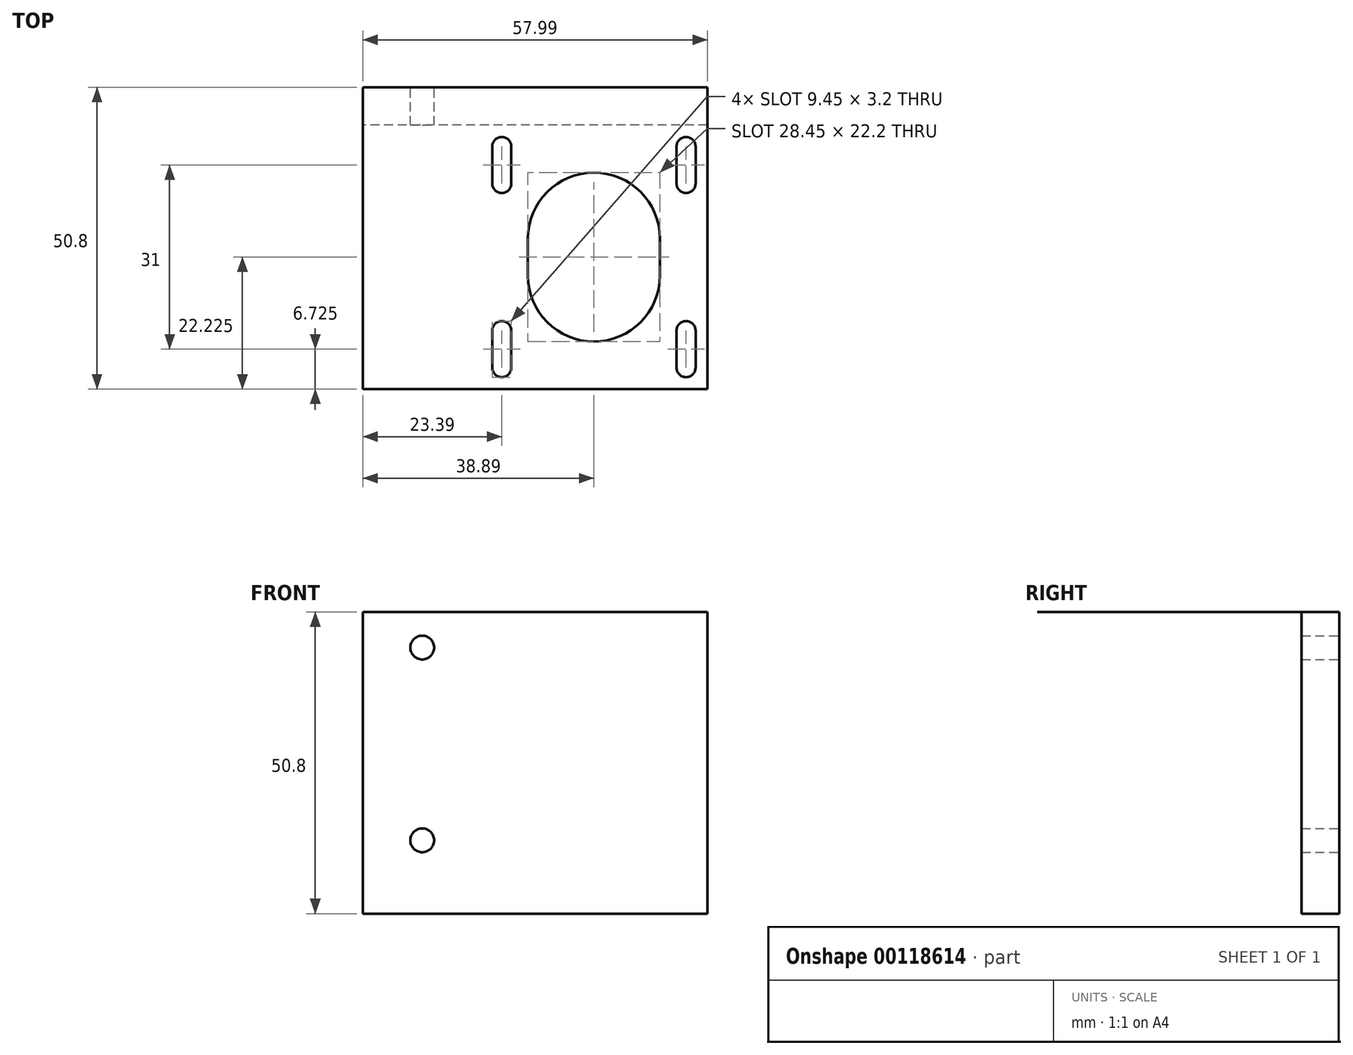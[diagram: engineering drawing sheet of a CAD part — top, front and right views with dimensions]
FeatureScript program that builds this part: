
annotation { "Feature Type Name" : "Feature", "Feature Type Description" : "" }
export const myFeature = defineFeature(function(context is Context, id is Id, definition is map)
    precondition{}
    {
        {
            var Q0;
            Q0=qCreatedBy(makeId("Top.planeOp"),FACE);
            var sketch = newSketch(context, id + "F0", { "sketchPlane" : qUnion([Q0])});
            skCircle(sketch, "E0", {"center": v(0, 0) * mm, "radius": 11.1 * mm});
            skCircle(sketch, "E1", {"center": v(-15.5, -15.5) * mm, "radius": 1.6 * mm});
            skCircle(sketch, "E2", {"center": v(-15.5, 15.5) * mm, "radius": 1.6 * mm});
            skCircle(sketch, "E3", {"center": v(15.5, 15.5) * mm, "radius": 1.6 * mm});
            skCircle(sketch, "E4", {"center": v(15.5, -15.5) * mm, "radius": 1.6 * mm});
            skLineSegment(sketch, "E5", {"start": v(15.5, -15.5) * mm, "end": v(-15.5, -15.5) * mm, "construction": true});
            skPoint(sketch, "E6", {"position": v(0, -15.5) * mm});
            skLineSegment(sketch, "E7", {"start": v(15.5, 15.5) * mm, "end": v(15.5, -15.5) * mm, "construction": true});
            skPoint(sketch, "E8", {"position": v(15.5, 0) * mm});
            skLineSegment(sketch, "E9.bottom", {"start": v(-38.9, 25.45) * mm, "end": v(19.1, 25.45) * mm});
            skLineSegment(sketch, "E9.top", {"start": v(-38.89, -25.35) * mm, "end": v(19.1, -25.35) * mm});
            skLineSegment(sketch, "E9.left", {"start": v(-38.9, 25.45) * mm, "end": v(-38.89, -25.35) * mm});
            skLineSegment(sketch, "E9.right", {"start": v(19.1, 25.45) * mm, "end": v(19.1, -25.35) * mm});
            skLineSegment(sketch, "E10", {"start": v(19.1, 19.1) * mm, "end": v(-38.9, 19.1) * mm});
            skCircle(sketch, "E11", {"center": v(0, -6.25) * mm, "radius": 11.1 * mm});
            skLineSegment(sketch, "E12", {"start": v(-11.1, -6.25) * mm, "end": v(-11.1, 0) * mm});
            skLineSegment(sketch, "E13", {"start": v(11.1, 0) * mm, "end": v(11.1, -6.25) * mm});
            skLineSegment(sketch, "E14", {"start": v(0, 0) * mm, "end": v(0, -6.25) * mm, "construction": true});
            skCircle(sketch, "E15", {"center": v(-15.5, 9.25) * mm, "radius": 1.6 * mm});
            skCircle(sketch, "E16", {"center": v(-15.5, -21.75) * mm, "radius": 1.6 * mm});
            skCircle(sketch, "E17", {"center": v(15.5, -21.75) * mm, "radius": 1.6 * mm});
            skCircle(sketch, "E18", {"center": v(15.5, 9.25) * mm, "radius": 1.6 * mm});
            skLineSegment(sketch, "E19", {"start": v(-15.5, 15.5) * mm, "end": v(-15.5, 9.25) * mm, "construction": true});
            skLineSegment(sketch, "E20", {"start": v(-15.5, -15.5) * mm, "end": v(-15.5, -21.75) * mm, "construction": true});
            skLineSegment(sketch, "E21", {"start": v(-17.1, 15.5) * mm, "end": v(-17.1, 9.25) * mm});
            skLineSegment(sketch, "E22", {"start": v(-13.9, 15.5) * mm, "end": v(-13.9, 9.25) * mm});
            skLineSegment(sketch, "E23", {"start": v(13.9, 15.5) * mm, "end": v(13.9, 9.25) * mm});
            skLineSegment(sketch, "E24", {"start": v(17.1, 15.5) * mm, "end": v(17.1, 9.25) * mm});
            skLineSegment(sketch, "E25", {"start": v(13.9, -21.75) * mm, "end": v(13.9, -15.5) * mm});
            skLineSegment(sketch, "E26", {"start": v(17.1, -15.5) * mm, "end": v(17.1, -21.75) * mm});
            skLineSegment(sketch, "E27", {"start": v(-17.1, -15.5) * mm, "end": v(-17.1, -21.75) * mm});
            skLineSegment(sketch, "E28", {"start": v(-13.9, -15.5) * mm, "end": v(-13.9, -21.75) * mm});
            skCircle(sketch, "E29", {"center": v(0, 0) * mm, "radius": 6.37 * mm, "construction": true});
            skPoint(sketch, "E30", {"position": v(-28.9, 25.45) * mm});
            skLineSegment(sketch, "E31", {"start": v(-6.37, 5) * mm, "end": v(-6.36, -5.45) * mm});
            skLineSegment(sketch, "E32", {"start": v(-18.9, 25.45) * mm, "end": v(-18.89, -25.35) * mm, "construction": true});
            skSolve(sketch);
        }
        {
            var Q0;
            {var subQ0=sQuery(id+"F0.wireOp",EDGE,"E9.bottom");Q0=makeQuery(id+"F0.imprint","IMPRINT",FACE,{"disambiguationData":[TD([[makeQuery(id+"F0.imprint","IMPRINT",EDGE,{"derivedFrom":subQ0}),-1.0]])]});}
            var Q1;
            {var subQ15=sQuery(id+"F0.wireOp",EDGE,"E9.top");Q1=makeQuery(id+"F0.imprint","IMPRINT",FACE,{"disambiguationData":[TD([[makeQuery(id+"F0.imprint","IMPRINT",EDGE,{"derivedFrom":subQ15}),1.0]])]});}
            extrude(context, id + "F1", {"entities" : qUnion([Q0, Q1]), "depth" : 1 / 101.6 * mm});
        }
        {
            var Q0;
            {var subQ0=sQuery(id+"F0.wireOp",EDGE,"E9.bottom");Q0=makeQuery(id+"F0.imprint","IMPRINT",FACE,{"disambiguationData":[TD([[makeQuery(id+"F0.imprint","IMPRINT",EDGE,{"derivedFrom":subQ0}),-1.0]])]});}
            extrude(context, id + "F2", {"entities" : qUnion([Q0]), "operationType" : NewBodyOperationType.ADD, "oppositeDirection" : true, "depth" : 50.8 * mm - 1 / 101.6 * mm});
        }
        {
            var Q0;
            {var subQ0=sQuery(id+"F0.wireOp",EDGE,"E9.bottom");Q0=makeQuery(id+"F2.boolean.opBoolean","MERGE",FACE,{"derivedFrom":[makeQuery(id+"F1.opExtrude","SWEPT_FACE",FACE,{"disambiguationData":[OSD([subQ0])]}),makeQuery(id+"F2.opExtrude","SWEPT_FACE",FACE,{"disambiguationData":[OSD([subQ0])]})]});}
            var sketch = newSketch(context, id + "F3", { "sketchPlane" : qUnion([Q0])});
            skPoint(sketch, "E33.0", {"position": v(28.9, 0) * mm});
            skLineSegment(sketch, "E34", {"start": v(28.9, 0) * mm, "end": v(28.9, -44.45) * mm, "construction": true});
            skCircle(sketch, "E35", {"center": v(28.9, -6) * mm, "radius": 2 * mm});
            skCircle(sketch, "E36", {"center": v(28.9, -38.45) * mm, "radius": 2 * mm});
            skSolve(sketch);
        }
        {
            var Q0;
            {var subQ0=sQuery(id+"F3.wireOp",EDGE,"759ac89f-ade1-41fe-b8ab-2c2021a6f035.0");var subQ1=sQuery(id+"F3.wireOp",EDGE,"AExLRClv-sBXU-07wI-fARC-cfbf8bb9NdPH");var subQ2=makeQuery(id+"F3.imprint","INTERSECT",VERTEX,{"derivedFrom":[subQ1,subQ0]});Q0=makeQuery(id+"F3.imprint","IMPRINT",FACE,{"disambiguationData":[TD([[makeQuery(id+"F3.imprint","IMPRINT",EDGE,{"disambiguationData":[TD([[subQ2,-1.0]])],"derivedFrom":subQ1}),-1.0]])]});}
            var Q1;
            Q1=makeQuery(id+"F3.imprint","IMPRINT",FACE,{"disambiguationData":[TD([[makeQuery(id+"F3.imprint","IMPRINT",EDGE,{"derivedFrom":sQuery(id+"F3.wireOp",EDGE,"E35")}),1.0]])]});
            var Q2;
            Q2=makeQuery(id+"F3.imprint","IMPRINT",FACE,{"disambiguationData":[TD([[makeQuery(id+"F3.imprint","IMPRINT",EDGE,{"derivedFrom":sQuery(id+"F3.wireOp",EDGE,"E36")}),1.0]])]});
            extrude(context, id + "F4", {"entities" : qUnion([Q0, Q1, Q2]), "operationType" : NewBodyOperationType.REMOVE, "endBound" : BoundingType.THROUGH_ALL, "oppositeDirection" : true, "depth" : 25 * mm});
        }
    });
